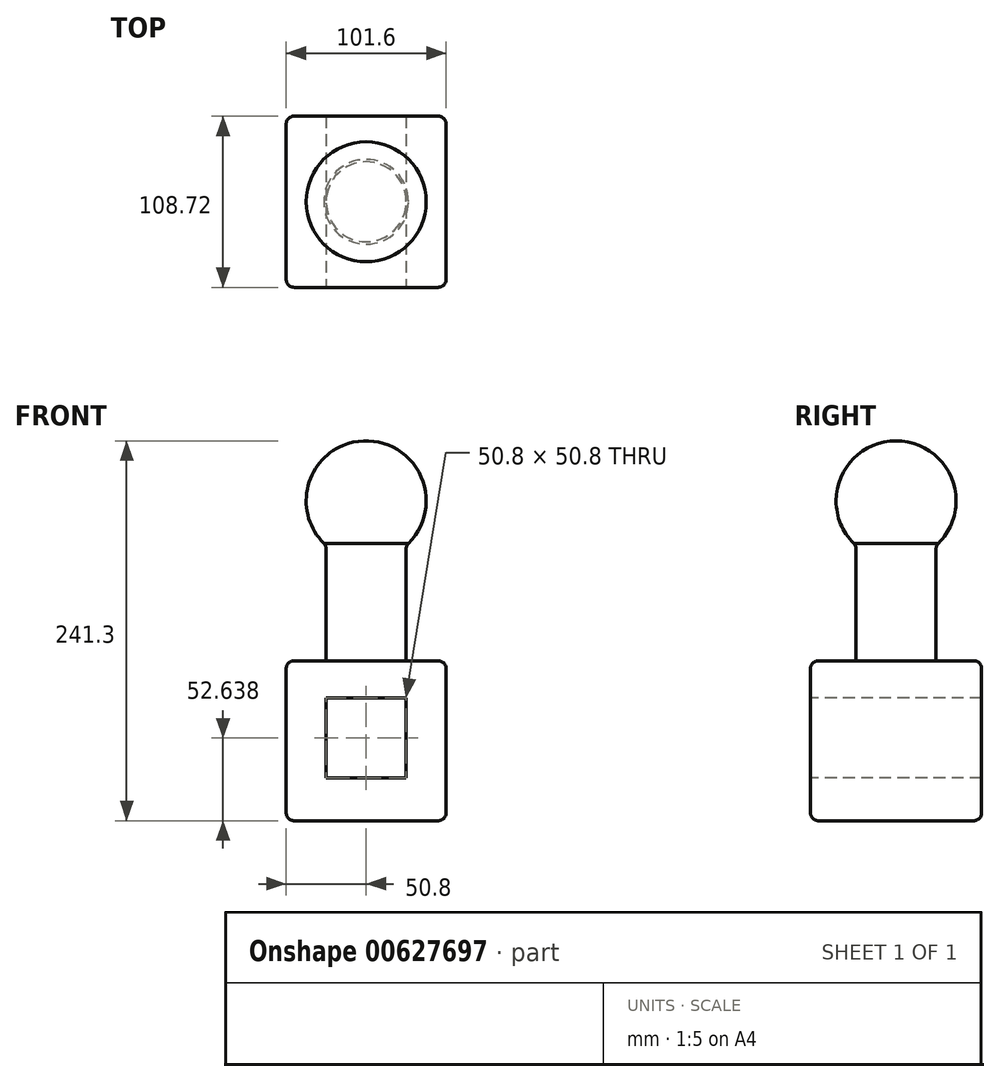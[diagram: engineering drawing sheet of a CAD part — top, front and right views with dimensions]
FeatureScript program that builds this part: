
annotation { "Feature Type Name" : "Feature", "Feature Type Description" : "" }
export const myFeature = defineFeature(function(context is Context, id is Id, definition is map)
    precondition{}
    {
        {
            var Q0;
            Q0=qCreatedBy(makeId("Top.planeOp"),FACE);
            var sketch = newSketch(context, id + "F0", { "sketchPlane" : qUnion([Q0])});
            skLineSegment(sketch, "E0.bottom", {"start": v(50.8, -54.36) * mm, "end": v(-50.8, -54.36) * mm});
            skLineSegment(sketch, "E0.top", {"start": v(50.8, 54.36) * mm, "end": v(-50.8, 54.36) * mm});
            skLineSegment(sketch, "E0.left", {"start": v(50.8, -54.36) * mm, "end": v(50.8, 54.36) * mm});
            skLineSegment(sketch, "E0.right", {"start": v(-50.8, -54.36) * mm, "end": v(-50.8, 54.36) * mm});
            skPoint(sketch, "E0.middle", {"position": v(0, 0) * mm});
            skSolve(sketch);
        }
        {
            var Q0;
            Q0 = qSketchRegion(id + "F0", true);
            extrude(context, id + "F1", {"entities" : qUnion([Q0]), "depth" : 101.6 * mm, "offsetDistance" : 25.4 * mm});
        }
        {
            var Q0;
            Q0=makeQuery(id+"F1.opExtrude","CAP_FACE",FACE,{"disambiguationData":[OSD([sQuery(id+"F0.wireOp",EDGE,"E0.bottom"),sQuery(id+"F0.wireOp",EDGE,"E0.top"),sQuery(id+"F0.wireOp",EDGE,"E0.left"),sQuery(id+"F0.wireOp",EDGE,"E0.right")])],"isStart":false});
            var sketch = newSketch(context, id + "F2", { "sketchPlane" : qUnion([Q0])});
            skCircle(sketch, "E1", {"center": v(0, 0) * mm, "radius": 25.4 * mm});
            skSolve(sketch);
        }
        {
            var Q0;
            Q0=makeQuery(id+"F2.imprint","IMPRINT",FACE,{"disambiguationData":[TD([[makeQuery(id+"F2.imprint","IMPRINT",EDGE,{"derivedFrom":sQuery(id+"F2.wireOp",EDGE,"E1")}),1.0]])]});
            extrude(context, id + "F3", {"entities" : qUnion([Q0]), "operationType" : NewBodyOperationType.ADD, "depth" : 101.6 * mm, "offsetDistance" : 25.4 * mm});
        }
        {
            var Q0;
            Q0=makeQuery(id+"F3.opExtrude","CAP_FACE",FACE,{"disambiguationData":[OSD([sQuery(id+"F2.wireOp",EDGE,"E1")])],"isStart":false});
            var sketch = newSketch(context, id + "F4", { "sketchPlane" : qUnion([Q0])});
            skSolve(sketch);
        }
        {
            var Q0;
            Q0=makeQuery(id+"F4.imprint","IMPRINT",FACE,{"disambiguationData":[TD([[makeQuery(id+"F4.imprint","IMPRINT",EDGE,{"derivedFrom":makeQuery(id+"F3.opExtrude","CAP_EDGE",EDGE,{"disambiguationData":[OSD([sQuery(id+"F2.wireOp",EDGE,"E1")])],"isStart":false})}),1.0]])]});
            var sketch = newSketch(context, id + "F5", { "sketchPlane" : qUnion([Q0])});
            skArc(sketch, "E2", {"start": v(0, -38.1) * mm, "mid": v(38.1, 0) * mm, "end": v(0, 38.1) * mm});
            skLineSegment(sketch, "E3", {"start": v(0, 38.1) * mm, "end": v(0, -38.1) * mm});
            skSolve(sketch);
        }
        {
            var Q0;
            {var subQ0=sQuery(id+"F5.wireOp",EDGE,"E2");Q0=makeQuery(id+"F5.imprint","IMPRINT",FACE,{"disambiguationData":[TD([[makeQuery(id+"F5.imprint","IMPRINT",EDGE,{"derivedFrom":subQ0}),1.0]])]});}
            var Q1;
            {var subQ0=sQuery(id+"F5.wireOp",EDGE,"E3");var subQ1=makeQuery(id+"F4.imprint","IMPRINT",EDGE,{"derivedFrom":makeQuery(id+"F3.opExtrude","CAP_EDGE",EDGE,{"disambiguationData":[OSD([sQuery(id+"F2.wireOp",EDGE,"E1")])],"isStart":false})});var subQ2=makeQuery(id+"F5.imprint","INTERSECT",VERTEX,{"disambiguationData":[OD(0.0)],"derivedFrom":[subQ1,subQ0]});Q1=makeQuery(id+"F5.imprint","IMPRINT",FACE,{"disambiguationData":[TD([[makeQuery(id+"F5.imprint","IMPRINT",EDGE,{"disambiguationData":[TD([[subQ2,-1.0]])],"derivedFrom":subQ0}),1.0]])]});}
            var Q2;
            Q2=sQuery(id+"F5.wireOp",EDGE,"E3");
            revolve(context, id + "F6", {"operationType" : NewBodyOperationType.ADD, "entities" : qUnion([Q0, Q1]), "axis" : qUnion([Q2]), "revolveType" : RevolveType.FULL});
        }
        {
            var Q0;
            Q0=makeQuery(id+"F1.opExtrude","SWEPT_FACE",FACE,{"disambiguationData":[OSD([sQuery(id+"F0.wireOp",EDGE,"E0.bottom")])]});
            var sketch = newSketch(context, id + "F7", { "sketchPlane" : qUnion([Q0])});
            skLineSegment(sketch, "E4", {"start": v(50.8, 50.8) * mm, "end": v(0, 50.8) * mm});
            skSolve(sketch);
        }
        {
            var Q0;
            {var subQ0=sQuery(id+"F0.wireOp",EDGE,"E0.bottom");var subQ1=makeQuery(id+"F1.opExtrude","CAP_EDGE",EDGE,{"disambiguationData":[OSD([subQ0])],"isStart":true});Q0=makeQuery(id+"F7.imprint","IMPRINT",FACE,{"disambiguationData":[TD([[makeQuery(id+"F7.imprint","IMPRINT",EDGE,{"derivedFrom":subQ1}),-1.0]])]});}
            var sketch = newSketch(context, id + "F8", { "sketchPlane" : qUnion([Q0])});
            skLineSegment(sketch, "E5.bottom", {"start": v(25.4, 27.24) * mm, "end": v(-25.4, 27.24) * mm});
            skLineSegment(sketch, "E5.top", {"start": v(25.4, 78.04) * mm, "end": v(-25.4, 78.04) * mm});
            skLineSegment(sketch, "E5.left", {"start": v(25.4, 27.24) * mm, "end": v(25.4, 78.04) * mm});
            skLineSegment(sketch, "E5.right", {"start": v(-25.4, 27.24) * mm, "end": v(-25.4, 78.04) * mm});
            skPoint(sketch, "E5.middle", {"position": v(0, 52.64) * mm});
            skSolve(sketch);
        }
        {
            var Q0;
            Q0 = qSketchRegion(id + "F8", true);
            extrude(context, id + "F9", {"entities" : qUnion([Q0]), "operationType" : NewBodyOperationType.REMOVE, "oppositeDirection" : true, "depth" : 127 * mm, "offsetDistance" : 25.4 * mm});
        }
        {
            var Q0;
            Q0=makeQuery(id+"F1.opExtrude","CAP_EDGE",EDGE,{"disambiguationData":[OSD([sQuery(id+"F0.wireOp",EDGE,"E0.bottom")])],"isStart":false});
            var Q1;
            Q1=makeQuery(id+"F1.opExtrude","CAP_EDGE",EDGE,{"disambiguationData":[OSD([sQuery(id+"F0.wireOp",EDGE,"E0.left")])],"isStart":false});
            var Q2;
            Q2=makeQuery(id+"F1.opExtrude","SWEPT_EDGE",EDGE,{"disambiguationData":[OSD([sQuery(id+"F0.wireOp",EDGE,"E0.bottom"),sQuery(id+"F0.wireOp",EDGE,"E0.left")])]});
            var Q3;
            Q3=makeQuery(id+"F1.opExtrude","CAP_EDGE",EDGE,{"disambiguationData":[OSD([sQuery(id+"F0.wireOp",EDGE,"E0.right")])],"isStart":false});
            var Q4;
            Q4=makeQuery(id+"F1.opExtrude","CAP_EDGE",EDGE,{"disambiguationData":[OSD([sQuery(id+"F0.wireOp",EDGE,"E0.top")])],"isStart":false});
            var Q5;
            Q5=makeQuery(id+"F1.opExtrude","SWEPT_EDGE",EDGE,{"disambiguationData":[OSD([sQuery(id+"F0.wireOp",EDGE,"E0.bottom"),sQuery(id+"F0.wireOp",EDGE,"E0.right")])]});
            var Q6;
            Q6=makeQuery(id+"F1.opExtrude","CAP_EDGE",EDGE,{"disambiguationData":[OSD([sQuery(id+"F0.wireOp",EDGE,"E0.bottom")])],"isStart":true});
            var Q7;
            Q7=makeQuery(id+"F1.opExtrude","CAP_EDGE",EDGE,{"disambiguationData":[OSD([sQuery(id+"F0.wireOp",EDGE,"E0.left")])],"isStart":true});
            var Q8;
            Q8=makeQuery(id+"F1.opExtrude","SWEPT_EDGE",EDGE,{"disambiguationData":[OSD([sQuery(id+"F0.wireOp",EDGE,"E0.top"),sQuery(id+"F0.wireOp",EDGE,"E0.left")])]});
            var Q9;
            Q9=makeQuery(id+"F1.opExtrude","SWEPT_EDGE",EDGE,{"disambiguationData":[OSD([sQuery(id+"F0.wireOp",EDGE,"E0.top"),sQuery(id+"F0.wireOp",EDGE,"E0.right")])]});
            var Q10;
            Q10=makeQuery(id+"F1.opExtrude","CAP_EDGE",EDGE,{"disambiguationData":[OSD([sQuery(id+"F0.wireOp",EDGE,"E0.top")])],"isStart":true});
            var Q11;
            Q11=makeQuery(id+"F1.opExtrude","CAP_EDGE",EDGE,{"disambiguationData":[OSD([sQuery(id+"F0.wireOp",EDGE,"E0.right")])],"isStart":true});
            var Q12;
            Q12=makeQuery(id+"F3.opExtrude","CAP_EDGE",EDGE,{"disambiguationData":[OSD([sQuery(id+"F2.wireOp",EDGE,"E1")])],"isStart":true});
            var Q13;
            Q13=makeQuery(id+"F6.boolean.opBoolean","INTERSECT",EDGE,{"derivedFrom":[makeQuery(id+"F3.opExtrude","SWEPT_FACE",FACE,{"disambiguationData":[OSD([sQuery(id+"F2.wireOp",EDGE,"E1")])]}),makeQuery(id+"F6.opRevolve","SWEPT_FACE",FACE,{"disambiguationData":[OSD([sQuery(id+"F5.wireOp",EDGE,"E2")])]})]});
            fillet(context, id + "F10", {"entities" : qUnion([Q0, Q1, Q2, Q3, Q4, Q5, Q6, Q7, Q8, Q9, Q10, Q11, Q12, Q13]), "radius" : 5.08 * mm, "tangentPropagation" : true, "allowEdgeOverflow" : false});
        }
    });
